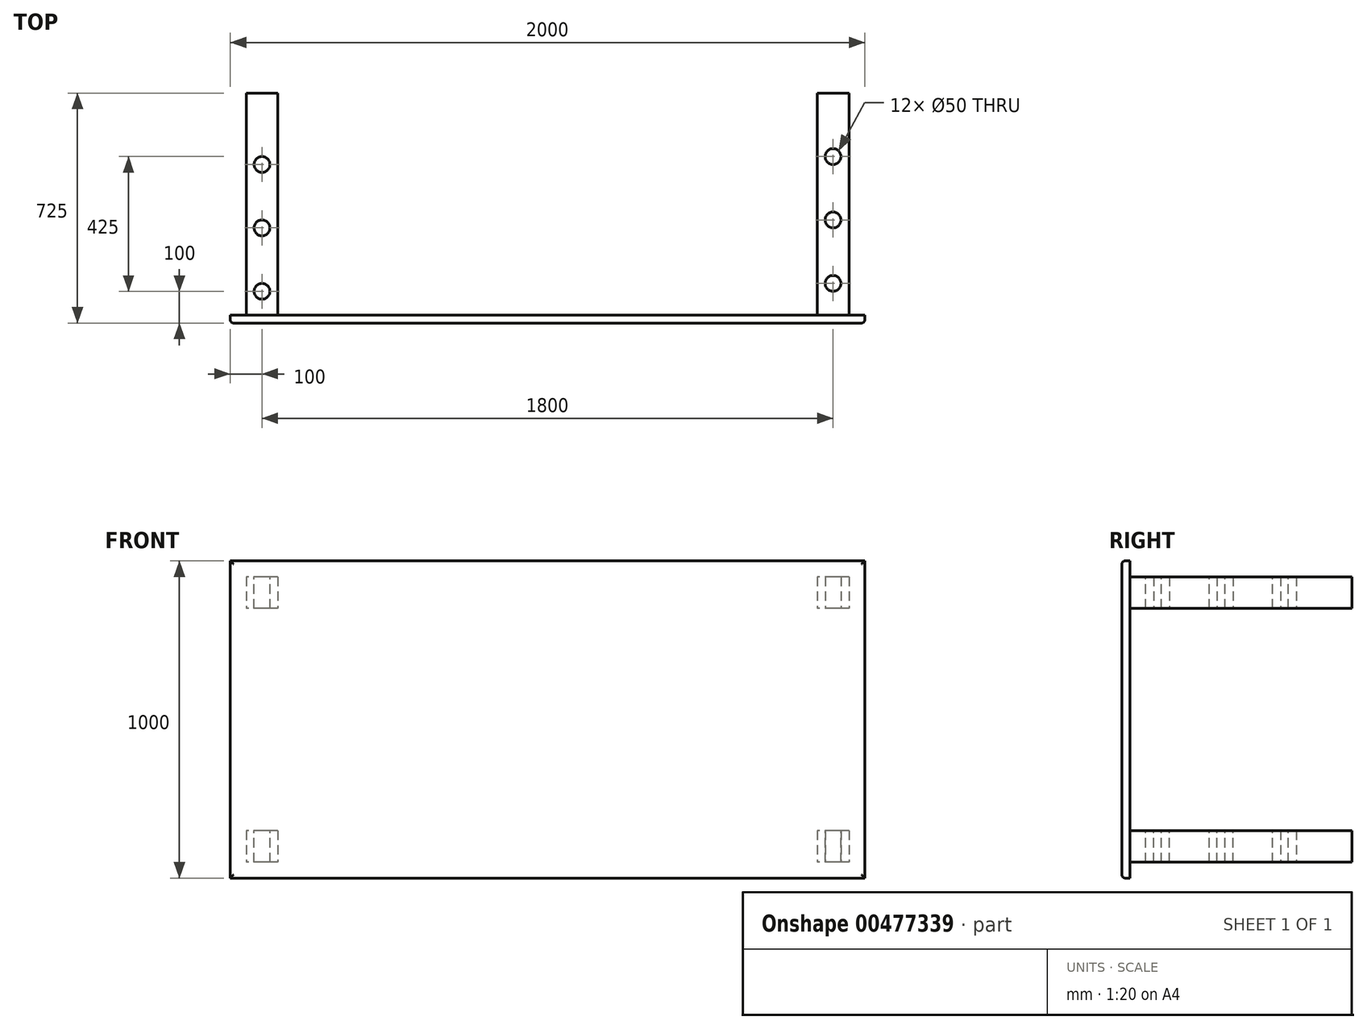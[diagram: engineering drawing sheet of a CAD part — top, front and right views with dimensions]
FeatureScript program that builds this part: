
annotation { "Feature Type Name" : "Feature", "Feature Type Description" : "" }
export const myFeature = defineFeature(function(context is Context, id is Id, definition is map)
    precondition{}
    {
        {
            var Q0;
            Q0=qCreatedBy(makeId("Front.planeOp"),FACE);
            var sketch = newSketch(context, id + "F0", { "sketchPlane" : qUnion([Q0])});
            skLineSegment(sketch, "E0.bottom", {"start": v(0, 0) * mm, "end": v(2000, 0) * mm});
            skLineSegment(sketch, "E0.top", {"start": v(0, 1000) * mm, "end": v(2000, 1000) * mm});
            skLineSegment(sketch, "E0.left", {"start": v(0, 0) * mm, "end": v(0, 1000) * mm});
            skLineSegment(sketch, "E0.right", {"start": v(2000, 0) * mm, "end": v(2000, 1000) * mm});
            skSolve(sketch);
        }
        {
            var Q0;
            Q0 = qSketchRegion(id + "F0", true);
            extrude(context, id + "F1", {"entities" : qUnion([Q0]), "depth" : 25 * mm});
        }
        {
            var Q0;
            Q0=makeQuery(id+"F1.opExtrude","CAP_FACE",FACE,{"disambiguationData":[OSD([sQuery(id+"F0.wireOp",EDGE,"E0.bottom"),sQuery(id+"F0.wireOp",EDGE,"E0.top"),sQuery(id+"F0.wireOp",EDGE,"E0.left"),sQuery(id+"F0.wireOp",EDGE,"E0.right")])],"isStart":true});
            var sketch = newSketch(context, id + "F2", { "sketchPlane" : qUnion([Q0])});
            skLineSegment(sketch, "E1.bottom", {"start": v(-1950, 150) * mm, "end": v(-1850, 150) * mm});
            skLineSegment(sketch, "E1.top", {"start": v(-1950, 50) * mm, "end": v(-1850, 50) * mm});
            skLineSegment(sketch, "E1.left", {"start": v(-1950, 150) * mm, "end": v(-1950, 50) * mm});
            skLineSegment(sketch, "E1.right", {"start": v(-1850, 150) * mm, "end": v(-1850, 50) * mm});
            skLineSegment(sketch, "E2.bottom", {"start": v(-150, 150) * mm, "end": v(-50, 150) * mm});
            skLineSegment(sketch, "E2.top", {"start": v(-150, 50) * mm, "end": v(-50, 50) * mm});
            skLineSegment(sketch, "E2.left", {"start": v(-150, 150) * mm, "end": v(-150, 50) * mm});
            skLineSegment(sketch, "E2.right", {"start": v(-50, 150) * mm, "end": v(-50, 50) * mm});
            skLineSegment(sketch, "E3.bottom", {"start": v(-1950, 950) * mm, "end": v(-1850, 950) * mm});
            skLineSegment(sketch, "E3.top", {"start": v(-1950, 850) * mm, "end": v(-1850, 850) * mm});
            skLineSegment(sketch, "E3.left", {"start": v(-1950, 950) * mm, "end": v(-1950, 850) * mm});
            skLineSegment(sketch, "E3.right", {"start": v(-1850, 950) * mm, "end": v(-1850, 850) * mm});
            skLineSegment(sketch, "E4.bottom", {"start": v(-150, 950) * mm, "end": v(-50, 950) * mm});
            skLineSegment(sketch, "E4.top", {"start": v(-150, 850) * mm, "end": v(-50, 850) * mm});
            skLineSegment(sketch, "E4.left", {"start": v(-150, 950) * mm, "end": v(-150, 850) * mm});
            skLineSegment(sketch, "E4.right", {"start": v(-50, 950) * mm, "end": v(-50, 850) * mm});
            skSolve(sketch);
        }
        {
            var Q0;
            Q0 = qSketchRegion(id + "F2", true);
            extrude(context, id + "F3", {"entities" : qUnion([Q0]), "operationType" : NewBodyOperationType.ADD, "depth" : 700 * mm});
        }
        {
            var Q0;
            Q0=makeQuery(id+"F3.opExtrude","SWEPT_FACE",FACE,{"disambiguationData":[OSD([sQuery(id+"F2.wireOp",EDGE,"E1.top")])]});
            var sketch = newSketch(context, id + "F4", { "sketchPlane" : qUnion([Q0])});
            skCircle(sketch, "E5", {"center": v(1900, -500) * mm, "radius": 25 * mm});
            skCircle(sketch, "E6", {"center": v(0, 0) * mm, "radius": 25 * mm});
            skSolve(sketch);
        }
        {
            var Q0;
            Q0=makeQuery(id+"F4.imprint","IMPRINT",FACE,{"disambiguationData":[TD([[makeQuery(id+"F4.imprint","IMPRINT",EDGE,{"derivedFrom":sQuery(id+"F4.wireOp",EDGE,"E5")}),1.0]])]});
            extrude(context, id + "F5", {"entities" : qUnion([Q0]), "operationType" : NewBodyOperationType.REMOVE, "oppositeDirection" : true, "depth" : 2819 * mm});
        }
        {
            var Q0;
            Q0=makeQuery(id+"F3.opExtrude","SWEPT_FACE",FACE,{"disambiguationData":[OSD([sQuery(id+"F2.wireOp",EDGE,"E1.bottom")])]});
            var sketch = newSketch(context, id + "F6", { "sketchPlane" : qUnion([Q0])});
            skCircle(sketch, "E7", {"center": v(1900, 300) * mm, "radius": 25 * mm});
            skSolve(sketch);
        }
        {
            var Q0;
            Q0=makeQuery(id+"F6.imprint","IMPRINT",FACE,{"disambiguationData":[TD([[makeQuery(id+"F6.imprint","IMPRINT",EDGE,{"derivedFrom":sQuery(id+"F6.wireOp",EDGE,"E7")}),1.0]])]});
            extrude(context, id + "F7", {"entities" : qUnion([Q0]), "operationType" : NewBodyOperationType.REMOVE, "depth" : 2080 * mm});
        }
        {
            var Q0;
            Q0=makeQuery(id+"F3.opExtrude","SWEPT_FACE",FACE,{"disambiguationData":[OSD([sQuery(id+"F2.wireOp",EDGE,"E1.bottom")])]});
            var sketch = newSketch(context, id + "F8", { "sketchPlane" : qUnion([Q0])});
            skCircle(sketch, "E8", {"center": v(1900, 100) * mm, "radius": 25 * mm});
            skSolve(sketch);
        }
        {
            var Q0;
            Q0=makeQuery(id+"F8.imprint","IMPRINT",FACE,{"disambiguationData":[TD([[makeQuery(id+"F8.imprint","IMPRINT",EDGE,{"derivedFrom":sQuery(id+"F8.wireOp",EDGE,"E8")}),1.0]])]});
            extrude(context, id + "F9", {"entities" : qUnion([Q0]), "operationType" : NewBodyOperationType.REMOVE, "depth" : 773 * mm});
        }
        {
            var Q0;
            Q0=makeQuery(id+"F3.opExtrude","SWEPT_FACE",FACE,{"disambiguationData":[OSD([sQuery(id+"F2.wireOp",EDGE,"E4.bottom")])]});
            var sketch = newSketch(context, id + "F10", { "sketchPlane" : qUnion([Q0])});
            skCircle(sketch, "E9", {"center": v(100, 475) * mm, "radius": 25 * mm});
            skSolve(sketch);
        }
        {
            var Q0;
            Q0 = qSketchRegion(id + "F10", true);
            extrude(context, id + "F11", {"entities" : qUnion([Q0]), "operationType" : NewBodyOperationType.REMOVE, "oppositeDirection" : true, "depth" : 1331 * mm});
        }
        {
            var Q0;
            Q0=makeQuery(id+"F3.opExtrude","SWEPT_FACE",FACE,{"disambiguationData":[OSD([sQuery(id+"F2.wireOp",EDGE,"E4.bottom")])]});
            var sketch = newSketch(context, id + "F12", { "sketchPlane" : qUnion([Q0])});
            skCircle(sketch, "E10", {"center": v(100, 275) * mm, "radius": 25 * mm});
            skSolve(sketch);
        }
        {
            var Q0;
            Q0 = qSketchRegion(id + "F12", true);
            extrude(context, id + "F13", {"entities" : qUnion([Q0]), "operationType" : NewBodyOperationType.REMOVE, "oppositeDirection" : true, "depth" : 1200 * mm});
        }
        {
            var Q0;
            Q0=makeQuery(id+"F10.imprint","IMPRINT",FACE,{"disambiguationData":[TD([[makeQuery(id+"F10.imprint","IMPRINT",EDGE,{"derivedFrom":sQuery(id+"F10.wireOp",EDGE,"E9")}),-1.0]])]});
            var sketch = newSketch(context, id + "F14", { "sketchPlane" : qUnion([Q0])});
            skCircle(sketch, "E11", {"center": v(100, 75) * mm, "radius": 25 * mm});
            skSolve(sketch);
        }
        {
            var Q0;
            Q0 = qSketchRegion(id + "F14", true);
            extrude(context, id + "F15", {"entities" : qUnion([Q0]), "operationType" : NewBodyOperationType.REMOVE, "oppositeDirection" : true, "depth" : 1300 * mm});
        }
        {
            var Q0;
            Q0 = qSketchRegion(id + "F6", true);
            extrude(context, id + "F16", {"entities" : qUnion([Q0]), "operationType" : NewBodyOperationType.REMOVE, "oppositeDirection" : true, "depth" : 338 * mm});
        }
        {
            var Q0;
            Q0=makeQuery(id+"F3.opExtrude","SWEPT_FACE",FACE,{"disambiguationData":[OSD([sQuery(id+"F2.wireOp",EDGE,"E3.bottom")])]});
            var sketch = newSketch(context, id + "F17", { "sketchPlane" : qUnion([Q0])});
            skCircle(sketch, "E12", {"center": v(1900, 100) * mm, "radius": 25 * mm});
            skSolve(sketch);
        }
        {
            var Q0;
            Q0 = qSketchRegion(id + "F17", true);
            extrude(context, id + "F18", {"entities" : qUnion([Q0]), "operationType" : NewBodyOperationType.REMOVE, "oppositeDirection" : true, "depth" : 1300 * mm});
        }
        {
            var Q0;
            Q0=makeQuery(id+"F1.opExtrude","CAP_EDGE",EDGE,{"disambiguationData":[OSD([sQuery(id+"F0.wireOp",EDGE,"E0.bottom")])],"isStart":false});
            var Q1;
            Q1=makeQuery(id+"F1.opExtrude","CAP_EDGE",EDGE,{"disambiguationData":[OSD([sQuery(id+"F0.wireOp",EDGE,"E0.left")])],"isStart":false});
            var Q2;
            Q2=makeQuery(id+"F1.opExtrude","CAP_EDGE",EDGE,{"disambiguationData":[OSD([sQuery(id+"F0.wireOp",EDGE,"E0.top")])],"isStart":false});
            var Q3;
            Q3=makeQuery(id+"F1.opExtrude","CAP_EDGE",EDGE,{"disambiguationData":[OSD([sQuery(id+"F0.wireOp",EDGE,"E0.right")])],"isStart":false});
            fillet(context, id + "F19", {"entities" : qUnion([Q0, Q1, Q2, Q3]), "radius" : 10 * mm, "tangentPropagation" : true, "allowEdgeOverflow" : false});
        }
    });
